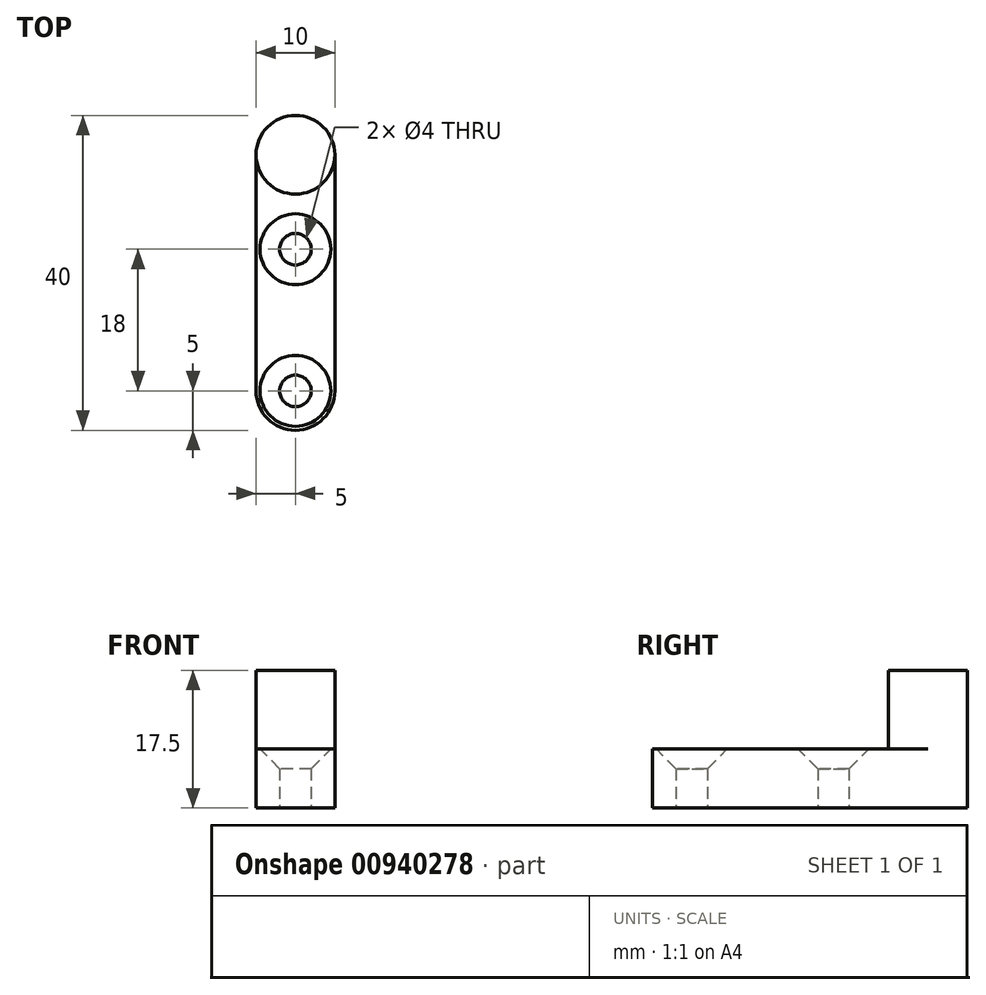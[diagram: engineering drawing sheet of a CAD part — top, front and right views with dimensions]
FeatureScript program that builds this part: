
annotation { "Feature Type Name" : "Feature", "Feature Type Description" : "" }
export const myFeature = defineFeature(function(context is Context, id is Id, definition is map)
    precondition{}
    {
        {
            var Q0;
            Q0=qCreatedBy(makeId("Top.planeOp"),FACE);
            var sketch = newSketch(context, id + "F0", { "sketchPlane" : qUnion([Q0])});
            skCircle(sketch, "E0", {"center": v(0, 0) * mm, "radius": 5 * mm});
            skLineSegment(sketch, "E1", {"start": v(0, 0) * mm, "end": v(4.63, 4.63) * mm, "construction": true});
            skLineSegment(sketch, "E2", {"start": v(5, 0) * mm, "end": v(5, -35) * mm});
            skLineSegment(sketch, "E3", {"start": v(5, -35) * mm, "end": v(0, -35) * mm});
            skLineSegment(sketch, "E4.MirrorCS", {"start": v(-5, 0) * mm, "end": v(-5, -35) * mm});
            skLineSegment(sketch, "E5.MirrorCS", {"start": v(-5, -35) * mm, "end": v(0, -35) * mm});
            skCircle(sketch, "E6", {"center": v(0, -30) * mm, "radius": 2 * mm});
            skCircle(sketch, "E7", {"center": v(0, -12) * mm, "radius": 2 * mm});
            skSolve(sketch);
        }
        {
            var Q0;
            {var subQ1=sQuery(id+"F0.wireOp",EDGE,"E2");Q0=makeQuery(id+"F0.imprint","IMPRINT",FACE,{"disambiguationData":[TD([[makeQuery(id+"F0.imprint","IMPRINT",EDGE,{"derivedFrom":subQ1}),-1.0]])]});}
            extrude(context, id + "F1", {"entities" : qUnion([Q0]), "depth" : 7.5 * mm, "offsetDistance" : 25 * mm});
        }
        {
            var Q0;
            {var subQ0=sQuery(id+"F0.wireOp",EDGE,"E0");var subQ1=makeQuery(id+"F0.imprint","INTERSECT",VERTEX,{"derivedFrom":[subQ0,sQuery(id+"F0.wireOp",EDGE,"E2")]});Q0=makeQuery(id+"F0.imprint","IMPRINT",FACE,{"disambiguationData":[TD([[makeQuery(id+"F0.imprint","IMPRINT",EDGE,{"disambiguationData":[TD([[subQ1,-1.0]])],"derivedFrom":subQ0}),1.0]])]});}
            extrude(context, id + "F2", {"entities" : qUnion([Q0]), "operationType" : NewBodyOperationType.ADD, "depth" : 17.5 * mm, "offsetDistance" : 25 * mm});
        }
        {
            var Q0;
            Q0=makeQuery(id+"F1.opExtrude","CAP_EDGE",EDGE,{"disambiguationData":[OSD([sQuery(id+"F0.wireOp",EDGE,"E7")])],"isStart":false});
            var Q1;
            Q1=makeQuery(id+"F1.opExtrude","CAP_EDGE",EDGE,{"disambiguationData":[OSD([sQuery(id+"F0.wireOp",EDGE,"E6")])],"isStart":false});
            chamfer(context, id + "F3", {"entities" : qUnion([Q0, Q1]), "chamferType" : ChamferType.OFFSET_ANGLE, "width" : 2.5 * mm, "oppositeDirection" : false, "angle" : 45 * degree, "tangentPropagation" : true});
        }
        {
            var Q0;
            Q0=makeQuery(id+"F1.opExtrude","SWEPT_EDGE",EDGE,{"disambiguationData":[OSD([sQuery(id+"F0.wireOp",EDGE,"E4.MirrorCS"),sQuery(id+"F0.wireOp",EDGE,"E5.MirrorCS")])]});
            var Q1;
            Q1=makeQuery(id+"F1.opExtrude","SWEPT_EDGE",EDGE,{"disambiguationData":[OSD([sQuery(id+"F0.wireOp",EDGE,"E2"),sQuery(id+"F0.wireOp",EDGE,"E3")])]});
            fillet(context, id + "F4", {"entities" : qUnion([Q0, Q1]), "radius" : 5 * mm, "tangentPropagation" : true, "allowEdgeOverflow" : false});
        }
    });
